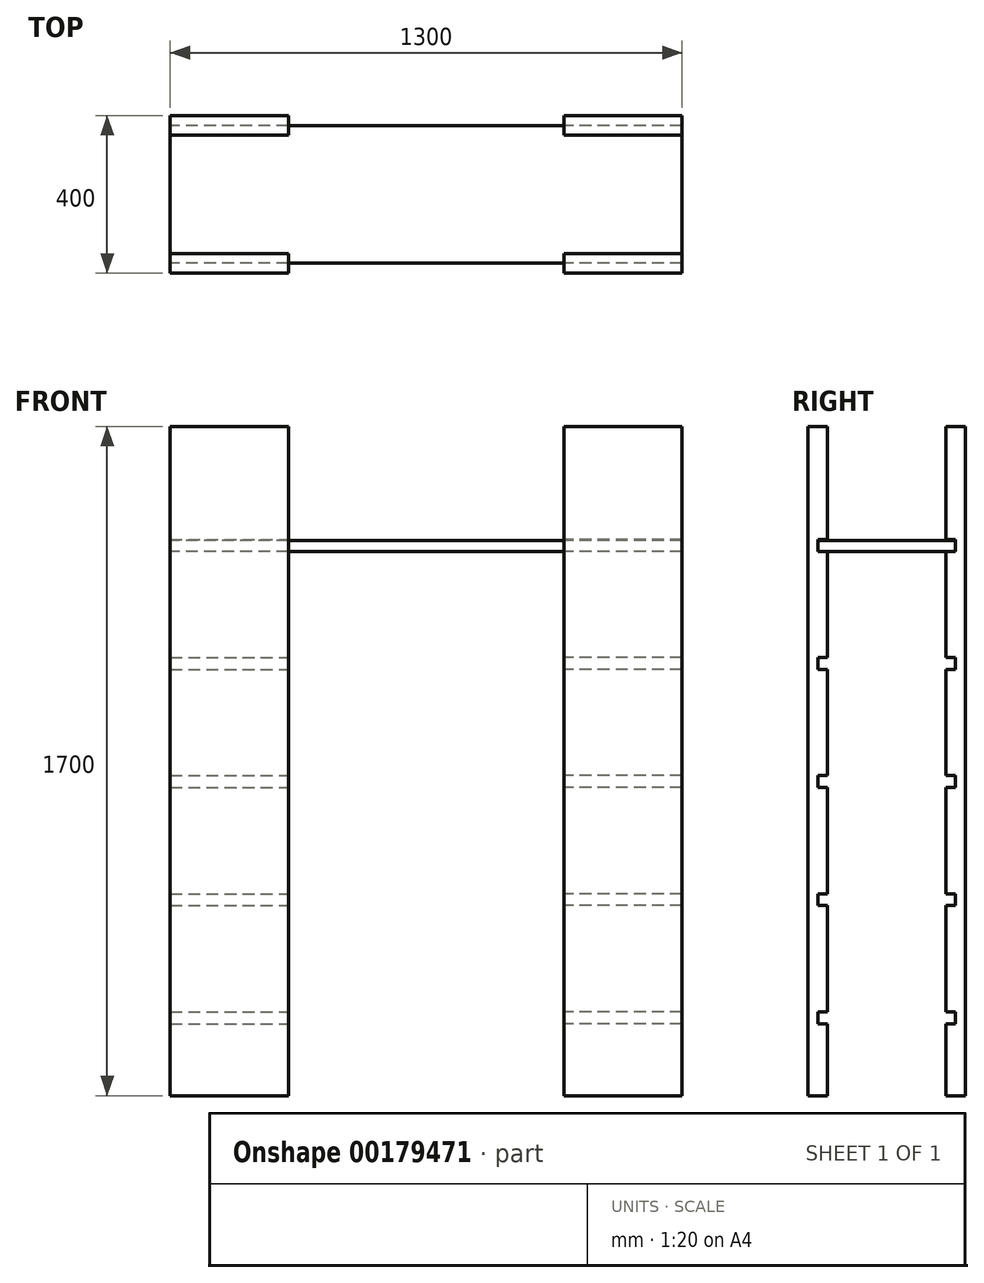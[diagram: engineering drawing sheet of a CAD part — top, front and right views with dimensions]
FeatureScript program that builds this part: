
annotation { "Feature Type Name" : "Feature", "Feature Type Description" : "" }
export const myFeature = defineFeature(function(context is Context, id is Id, definition is map)
    precondition{}
    {
        {
            var Q0;
            Q0=qCreatedBy(makeId("Top.planeOp"),FACE);
            var sketch = newSketch(context, id + "F0", { "sketchPlane" : qUnion([Q0])});
            skLineSegment(sketch, "E0.bottom", {"start": v(-650, 40.23) * mm, "end": v(-350, 40.23) * mm});
            skLineSegment(sketch, "E0.top", {"start": v(-650, -9.77) * mm, "end": v(-350, -9.77) * mm});
            skLineSegment(sketch, "E0.left", {"start": v(-650, 40.23) * mm, "end": v(-650, -9.77) * mm});
            skLineSegment(sketch, "E0.right", {"start": v(-350, 40.23) * mm, "end": v(-350, -9.77) * mm});
            skLineSegment(sketch, "E1.MirrorCS", {"start": v(650, 40.23) * mm, "end": v(350, 40.23) * mm});
            skLineSegment(sketch, "E2.MirrorCS", {"start": v(650, -9.77) * mm, "end": v(350, -9.77) * mm});
            skLineSegment(sketch, "E3.MirrorCS", {"start": v(650, 40.23) * mm, "end": v(650, -9.77) * mm});
            skLineSegment(sketch, "E4.MirrorCS", {"start": v(350, 40.23) * mm, "end": v(350, -9.77) * mm});
            skLineSegment(sketch, "E5.MirrorCS", {"start": v(-350, 340.23) * mm, "end": v(-350, 390.23) * mm});
            skLineSegment(sketch, "E6.MirrorCS", {"start": v(-650, 340.23) * mm, "end": v(-650, 390.23) * mm});
            skLineSegment(sketch, "E7.MirrorCS", {"start": v(-650, 340.23) * mm, "end": v(-350, 340.23) * mm});
            skLineSegment(sketch, "E8.MirrorCS", {"start": v(-650, 390.23) * mm, "end": v(-350, 390.23) * mm});
            skLineSegment(sketch, "E9.MirrorCS", {"start": v(350, 340.23) * mm, "end": v(350, 390.23) * mm});
            skLineSegment(sketch, "E10.MirrorCS", {"start": v(650, 340.23) * mm, "end": v(350, 340.23) * mm});
            skLineSegment(sketch, "E11.MirrorCS", {"start": v(650, 390.23) * mm, "end": v(350, 390.23) * mm});
            skLineSegment(sketch, "E12.MirrorCS", {"start": v(650, 340.23) * mm, "end": v(650, 390.23) * mm});
            skSolve(sketch);
        }
        {
            var Q0;
            Q0 = qSketchRegion(id + "F0", true);
            extrude(context, id + "F1", {"entities" : qUnion([Q0]), "oppositeDirection" : true, "depth" : 1700 * mm});
        }
        {
            var Q0;
            Q0=makeQuery(id+"F1.opExtrude","SWEPT_FACE",FACE,{"disambiguationData":[OSD([sQuery(id+"F0.wireOp",EDGE,"E10.MirrorCS")])]});
            var sketch = newSketch(context, id + "F2", { "sketchPlane" : qUnion([Q0])});
            skLineSegment(sketch, "E13.bottom", {"start": v(650, -1517) * mm, "end": v(350, -1517) * mm});
            skLineSegment(sketch, "E13.top", {"start": v(650, -1487) * mm, "end": v(350, -1487) * mm});
            skLineSegment(sketch, "E13.left", {"start": v(650, -1517) * mm, "end": v(650, -1487) * mm});
            skLineSegment(sketch, "E13.right", {"start": v(350, -1517) * mm, "end": v(350, -1487) * mm});
            skLineSegment(sketch, "E14.0.1.0", {"start": v(650, -1217) * mm, "end": v(350, -1217) * mm});
            skLineSegment(sketch, "E14.0.1.1", {"start": v(650, -1187) * mm, "end": v(350, -1187) * mm});
            skLineSegment(sketch, "E14.0.1.2", {"start": v(650, -1217) * mm, "end": v(650, -1187) * mm});
            skLineSegment(sketch, "E14.0.1.3", {"start": v(350, -1217) * mm, "end": v(350, -1187) * mm});
            skLineSegment(sketch, "E14.0.2.0", {"start": v(650, -917) * mm, "end": v(350, -917) * mm});
            skLineSegment(sketch, "E14.0.2.1", {"start": v(650, -887) * mm, "end": v(350, -887) * mm});
            skLineSegment(sketch, "E14.0.2.2", {"start": v(650, -917) * mm, "end": v(650, -887) * mm});
            skLineSegment(sketch, "E14.0.2.3", {"start": v(350, -917) * mm, "end": v(350, -887) * mm});
            skLineSegment(sketch, "E14.0.3.0", {"start": v(650, -617) * mm, "end": v(350, -617) * mm});
            skLineSegment(sketch, "E14.0.3.1", {"start": v(650, -587) * mm, "end": v(350, -587) * mm});
            skLineSegment(sketch, "E14.0.3.2", {"start": v(650, -617) * mm, "end": v(650, -587) * mm});
            skLineSegment(sketch, "E14.0.3.3", {"start": v(350, -617) * mm, "end": v(350, -587) * mm});
            skLineSegment(sketch, "E14.0.4.0", {"start": v(650, -317) * mm, "end": v(350, -317) * mm});
            skLineSegment(sketch, "E14.0.4.1", {"start": v(650, -287) * mm, "end": v(350, -287) * mm});
            skLineSegment(sketch, "E14.0.4.2", {"start": v(650, -317) * mm, "end": v(650, -287) * mm});
            skLineSegment(sketch, "E14.0.4.3", {"start": v(350, -317) * mm, "end": v(350, -287) * mm});
            skLineSegment(sketch, "E14.direction1", {"start": v(350, -1517) * mm, "end": v(375, -1517) * mm, "construction": true});
            skLineSegment(sketch, "E14.direction2", {"start": v(350, -1517) * mm, "end": v(350, -1217) * mm, "construction": true});
            skLineSegment(sketch, "E15.MirrorCS", {"start": v(-350, -1517) * mm, "end": v(-350, -1487) * mm});
            skLineSegment(sketch, "E16.MirrorCS", {"start": v(-350, -1517) * mm, "end": v(-350, -1217) * mm, "construction": true});
            skLineSegment(sketch, "E17.MirrorCS", {"start": v(-350, -1517) * mm, "end": v(-375, -1517) * mm, "construction": true});
            skLineSegment(sketch, "E18.MirrorCS", {"start": v(-350, -1217) * mm, "end": v(-350, -1187) * mm});
            skLineSegment(sketch, "E19.MirrorCS", {"start": v(-650, -1217) * mm, "end": v(-650, -1187) * mm});
            skLineSegment(sketch, "E20.MirrorCS", {"start": v(-650, -1517) * mm, "end": v(-650, -1487) * mm});
            skLineSegment(sketch, "E21.MirrorCS", {"start": v(-350, -617) * mm, "end": v(-350, -587) * mm});
            skLineSegment(sketch, "E22.MirrorCS", {"start": v(-650, -617) * mm, "end": v(-650, -587) * mm});
            skLineSegment(sketch, "E23.MirrorCS", {"start": v(-350, -317) * mm, "end": v(-350, -287) * mm});
            skLineSegment(sketch, "E24.MirrorCS", {"start": v(-650, -317) * mm, "end": v(-650, -287) * mm});
            skLineSegment(sketch, "E25.MirrorCS", {"start": v(-650, -917) * mm, "end": v(-650, -887) * mm});
            skLineSegment(sketch, "E26.MirrorCS", {"start": v(-350, -917) * mm, "end": v(-350, -887) * mm});
            skLineSegment(sketch, "E27.MirrorCS", {"start": v(-650, -1187) * mm, "end": v(-350, -1187) * mm});
            skLineSegment(sketch, "E28.MirrorCS", {"start": v(-650, -1217) * mm, "end": v(-350, -1217) * mm});
            skLineSegment(sketch, "E29.MirrorCS", {"start": v(-650, -1487) * mm, "end": v(-350, -1487) * mm});
            skLineSegment(sketch, "E30.MirrorCS", {"start": v(-650, -1517) * mm, "end": v(-350, -1517) * mm});
            skLineSegment(sketch, "E31.MirrorCS", {"start": v(-650, -587) * mm, "end": v(-350, -587) * mm});
            skLineSegment(sketch, "E32.MirrorCS", {"start": v(-650, -287) * mm, "end": v(-350, -287) * mm});
            skLineSegment(sketch, "E33.MirrorCS", {"start": v(-650, -317) * mm, "end": v(-350, -317) * mm});
            skLineSegment(sketch, "E34.MirrorCS", {"start": v(-650, -917) * mm, "end": v(-350, -917) * mm});
            skLineSegment(sketch, "E35.MirrorCS", {"start": v(-650, -887) * mm, "end": v(-350, -887) * mm});
            skLineSegment(sketch, "E36.MirrorCS", {"start": v(-650, -617) * mm, "end": v(-350, -617) * mm});
            skSolve(sketch);
        }
        {
            var Q0;
            Q0 = qSketchRegion(id + "F2", true);
            extrude(context, id + "F3", {"entities" : qUnion([Q0]), "operationType" : NewBodyOperationType.REMOVE, "oppositeDirection" : true, "depth" : 25 * mm});
        }
        {
            var Q0;
            Q0=makeQuery(id+"F1.opExtrude","SWEPT_FACE",FACE,{"disambiguationData":[OSD([sQuery(id+"F0.wireOp",EDGE,"E0.bottom")])]});
            var sketch = newSketch(context, id + "F4", { "sketchPlane" : qUnion([Q0])});
            skLineSegment(sketch, "E37.bottom", {"start": v(650, -1517) * mm, "end": v(350, -1517) * mm});
            skLineSegment(sketch, "E37.top", {"start": v(650, -1487) * mm, "end": v(350, -1487) * mm});
            skLineSegment(sketch, "E37.left", {"start": v(650, -1517) * mm, "end": v(650, -1487) * mm});
            skLineSegment(sketch, "E37.right", {"start": v(350, -1517) * mm, "end": v(350, -1487) * mm});
            skLineSegment(sketch, "E38.0.1.0", {"start": v(650, -1217) * mm, "end": v(350, -1217) * mm});
            skLineSegment(sketch, "E38.0.1.1", {"start": v(650, -1187) * mm, "end": v(350, -1187) * mm});
            skLineSegment(sketch, "E38.0.1.2", {"start": v(650, -1217) * mm, "end": v(650, -1187) * mm});
            skLineSegment(sketch, "E38.0.1.3", {"start": v(350, -1217) * mm, "end": v(350, -1187) * mm});
            skLineSegment(sketch, "E38.0.2.0", {"start": v(650, -917) * mm, "end": v(350, -917) * mm});
            skLineSegment(sketch, "E38.0.2.1", {"start": v(650, -887) * mm, "end": v(350, -887) * mm});
            skLineSegment(sketch, "E38.0.2.2", {"start": v(650, -917) * mm, "end": v(650, -887) * mm});
            skLineSegment(sketch, "E38.0.2.3", {"start": v(350, -917) * mm, "end": v(350, -887) * mm});
            skLineSegment(sketch, "E38.0.3.0", {"start": v(650, -617) * mm, "end": v(350, -617) * mm});
            skLineSegment(sketch, "E38.0.3.1", {"start": v(650, -587) * mm, "end": v(350, -587) * mm});
            skLineSegment(sketch, "E38.0.3.2", {"start": v(650, -617) * mm, "end": v(650, -587) * mm});
            skLineSegment(sketch, "E38.0.3.3", {"start": v(350, -617) * mm, "end": v(350, -587) * mm});
            skLineSegment(sketch, "E38.0.4.0", {"start": v(650, -317) * mm, "end": v(350, -317) * mm});
            skLineSegment(sketch, "E38.0.4.1", {"start": v(650, -287) * mm, "end": v(350, -287) * mm});
            skLineSegment(sketch, "E38.0.4.2", {"start": v(650, -317) * mm, "end": v(650, -287) * mm});
            skLineSegment(sketch, "E38.0.4.3", {"start": v(350, -317) * mm, "end": v(350, -287) * mm});
            skLineSegment(sketch, "E38.direction1", {"start": v(312.74, -1517) * mm, "end": v(350, -1517) * mm, "construction": true});
            skLineSegment(sketch, "E38.direction2", {"start": v(350, -1517) * mm, "end": v(350, -1217) * mm, "construction": true});
            skLineSegment(sketch, "E39.MirrorCS", {"start": v(-350, -1517) * mm, "end": v(-350, -1487) * mm});
            skLineSegment(sketch, "E40.MirrorCS", {"start": v(-312.74, -1517) * mm, "end": v(-350, -1517) * mm, "construction": true});
            skLineSegment(sketch, "E41.MirrorCS", {"start": v(-350, -1217) * mm, "end": v(-350, -1187) * mm});
            skLineSegment(sketch, "E42.MirrorCS", {"start": v(-350, -317) * mm, "end": v(-350, -287) * mm});
            skLineSegment(sketch, "E43.MirrorCS", {"start": v(-650, -1217) * mm, "end": v(-650, -1187) * mm});
            skLineSegment(sketch, "E44.MirrorCS", {"start": v(-650, -617) * mm, "end": v(-650, -587) * mm});
            skLineSegment(sketch, "E45.MirrorCS", {"start": v(-650, -317) * mm, "end": v(-650, -287) * mm});
            skLineSegment(sketch, "E46.MirrorCS", {"start": v(-650, -917) * mm, "end": v(-650, -887) * mm});
            skLineSegment(sketch, "E47.MirrorCS", {"start": v(-650, -1517) * mm, "end": v(-650, -1487) * mm});
            skLineSegment(sketch, "E48.MirrorCS", {"start": v(-350, -617) * mm, "end": v(-350, -587) * mm});
            skLineSegment(sketch, "E49.MirrorCS", {"start": v(-350, -917) * mm, "end": v(-350, -887) * mm});
            skLineSegment(sketch, "E50.MirrorCS", {"start": v(-650, -317) * mm, "end": v(-350, -317) * mm});
            skLineSegment(sketch, "E51.MirrorCS", {"start": v(-650, -587) * mm, "end": v(-350, -587) * mm});
            skLineSegment(sketch, "E52.MirrorCS", {"start": v(-650, -917) * mm, "end": v(-350, -917) * mm});
            skLineSegment(sketch, "E53.MirrorCS", {"start": v(-650, -1487) * mm, "end": v(-350, -1487) * mm});
            skLineSegment(sketch, "E54.MirrorCS", {"start": v(-650, -287) * mm, "end": v(-350, -287) * mm});
            skLineSegment(sketch, "E55.MirrorCS", {"start": v(-650, -617) * mm, "end": v(-350, -617) * mm});
            skLineSegment(sketch, "E56.MirrorCS", {"start": v(-650, -1217) * mm, "end": v(-350, -1217) * mm});
            skLineSegment(sketch, "E57.MirrorCS", {"start": v(-650, -887) * mm, "end": v(-350, -887) * mm});
            skLineSegment(sketch, "E58.MirrorCS", {"start": v(-650, -1517) * mm, "end": v(-350, -1517) * mm});
            skLineSegment(sketch, "E59.MirrorCS", {"start": v(-350, -1517) * mm, "end": v(-350, -1217) * mm, "construction": true});
            skLineSegment(sketch, "E60.MirrorCS", {"start": v(-650, -1187) * mm, "end": v(-350, -1187) * mm});
            skSolve(sketch);
        }
        {
            var Q0;
            Q0=makeQuery(id+"F3.boolean.opBoolean","COPY",FACE,{"derivedFrom":makeQuery(id+"F3.opExtrude","SWEPT_FACE",FACE,{"disambiguationData":[OSD([sQuery(id+"F2.wireOp",EDGE,"E14.0.4.0")])]})});
            var sketch = newSketch(context, id + "F5", { "sketchPlane" : qUnion([Q0])});
            skLineSegment(sketch, "E61", {"start": v(650, 340.23) * mm, "end": v(650, 365.23) * mm});
            skLineSegment(sketch, "E62.left", {"start": v(650, 365.23) * mm, "end": v(650, 15.23) * mm});
            skLineSegment(sketch, "E63.bottom", {"start": v(650, 365.23) * mm, "end": v(-650, 365.23) * mm});
            skLineSegment(sketch, "E63.top", {"start": v(650, 15.23) * mm, "end": v(-650, 15.23) * mm});
            skLineSegment(sketch, "E63.right", {"start": v(-650, 365.23) * mm, "end": v(-650, 15.23) * mm});
            skSolve(sketch);
        }
        {
            var Q0;
            Q0 = qSketchRegion(id + "F4", true);
            extrude(context, id + "F6", {"entities" : qUnion([Q0]), "operationType" : NewBodyOperationType.REMOVE, "oppositeDirection" : true, "depth" : 25 * mm});
        }
        {
            var Q0;
            Q0 = qSketchRegion(id + "F5", true);
            extrude(context, id + "F7", {"entities" : qUnion([Q0]), "depth" : 28 * mm});
        }
    });
